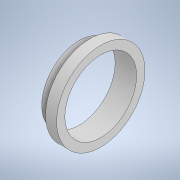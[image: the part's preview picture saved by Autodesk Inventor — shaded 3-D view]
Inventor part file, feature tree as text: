
AUTODESK INVENTOR PART (.ipt)
format: ipt  version: 2020 (Build 240168000, 168)  size: 116,736 bytes
history: native  units: mm
features: revolve x1, sketch x1
ambient origin geometry x8: Origin, YZ Plane, XZ Plane, XY Plane, X Axis, Y Axis, Z Axis, Center Point
bodies: 实体1 (feature_tree)
feature tree (2):
  revolve  "旋转1"  [1 undecoded]
  sketch  "草图1"  dims[d0=68.0mm d1=65.0mm d2=19.5mm d3=10.0mm d4=80.0mm d5=90.0deg]
note: 1 required parameter value undecoded (feature->parameter linkage not recoverable at this tier; creation-order binding heuristic only, values carry confidence <= 0.55)
